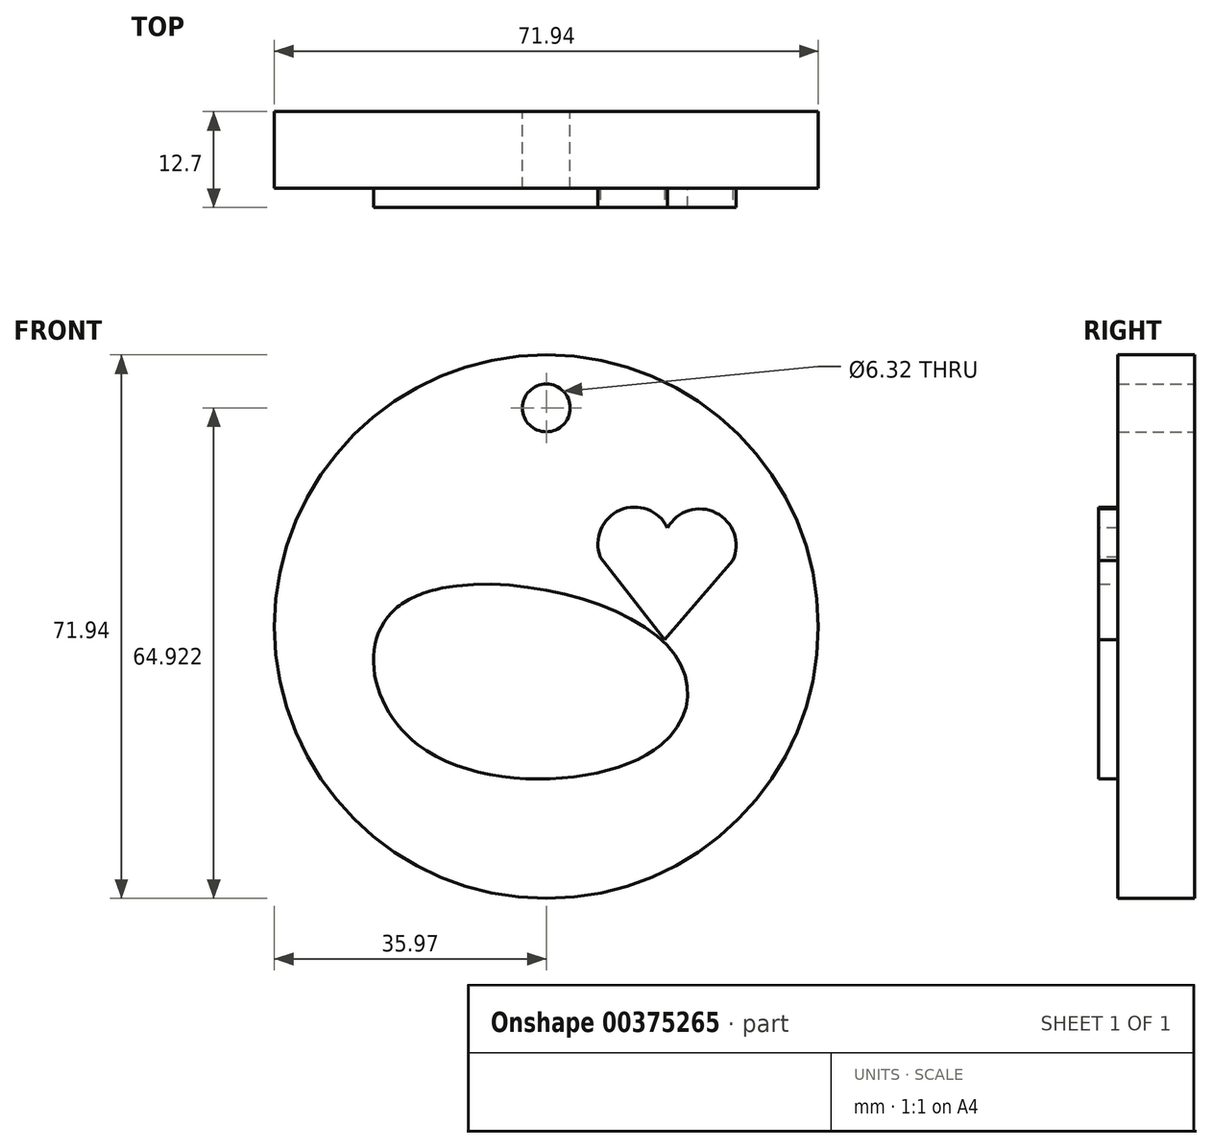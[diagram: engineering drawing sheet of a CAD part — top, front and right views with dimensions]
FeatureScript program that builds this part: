
annotation { "Feature Type Name" : "Feature", "Feature Type Description" : "" }
export const myFeature = defineFeature(function(context is Context, id is Id, definition is map)
    precondition{}
    {
        {
            var Q0;
            Q0=qCreatedBy(makeId("Front.planeOp"),FACE);
            var sketch = newSketch(context, id + "F0", { "sketchPlane" : qUnion([Q0])});
            skCircle(sketch, "E0", {"center": v(0, 0) * mm, "radius": 35.97 * mm});
            skSolve(sketch);
        }
        {
            var Q0;
            Q0=qSketchRegion(id+"F0",true);
            extrude(context, id + "F1", {"entities" : qUnion([Q0]), "depth" : 12.7 * mm});
        }
        {
            var Q0;
            Q0=makeQuery(id+"F1.opExtrude","CAP_FACE",FACE,{"disambiguationData":[OSD([sQuery(id+"F0.wireOp",EDGE,"E0")])],"isStart":false});
            var sketch = newSketch(context, id + "F2", { "sketchPlane" : qUnion([Q0])});
            skEllipticalArc(sketch, "E1", {});
            skPoint(sketch, "E2.2.internal.snap0", {"position": v(15.22, -15.6) * mm});
            skFitSpline(sketch, "E2", {"points": [v(-17, -15.6) * mm, v(15.22, -15.6) * mm, v(15.22, -1.73) * mm, v(-19.73, 2.56) * mm, v(-17, -15.6) * mm]});
            skArc(sketch, "E3", {"start": v(-17.8, 13.08) * mm, "mid": v(-24.21, 15.07) * mm, "end": v(-26.44, 8.74) * mm});
            skLineSegment(sketch, "E4", {"start": v(-26.44, 8.74) * mm, "end": v(-17.39, -1.73) * mm});
            skArc(sketch, "E5.MirrorCS", {"start": v(-17.8, 13.08) * mm, "mid": v(-11.5, 15.43) * mm, "end": v(-8.93, 9.22) * mm});
            skLineSegment(sketch, "E6.MirrorCS", {"start": v(-8.93, 9.22) * mm, "end": v(-17.39, -1.73) * mm});
            skArc(sketch, "E7.MirrorCS", {"start": v(16.02, 13.08) * mm, "mid": v(22.44, 15.07) * mm, "end": v(24.66, 8.74) * mm});
            skLineSegment(sketch, "E8.MirrorCS", {"start": v(24.66, 8.74) * mm, "end": v(15.61, -1.73) * mm});
            skLineSegment(sketch, "E9.MirrorCS", {"start": v(7.16, 9.22) * mm, "end": v(15.61, -1.73) * mm});
            skArc(sketch, "E10.MirrorCS", {"start": v(16.02, 13.08) * mm, "mid": v(9.73, 15.43) * mm, "end": v(7.16, 9.22) * mm});
            const initialGuessF2  = {"E1": [-0.0008881420638489816, -0.015604647807777988, 1, 0, 0.01610479690134306, 0.012966257095941073, 3.141592653589793, 0]};
            skSetInitialGuess(sketch, initialGuessF2);
            skSolve(sketch);
        }
        {
            var Q0;
            Q0=makeQuery(id+"F2.imprint","IMPRINT",FACE,{"disambiguationData":[TD([[makeQuery(id+"F2.imprint","IMPRINT",EDGE,{"derivedFrom":sQuery(id+"F2.wireOp",EDGE,"E7.MirrorCS")}),-1.0]])]});
            var Q1;
            Q1=makeQuery(id+"F2.imprint","IMPRINT",FACE,{"disambiguationData":[TD([[makeQuery(id+"F2.imprint","IMPRINT",EDGE,{"derivedFrom":sQuery(id+"F2.wireOp",EDGE,"E3")}),1.0]])]});
            var Q2;
            Q2=makeQuery(id+"F2.imprint","IMPRINT",FACE,{"disambiguationData":[TD([[makeQuery(id+"F2.imprint","IMPRINT",EDGE,{"derivedFrom":sQuery(id+"F2.wireOp",EDGE,"E1")}),1.0]])]});
            extrude(context, id + "F3", {"entities" : qUnion([Q0, Q1, Q2]), "operationType" : NewBodyOperationType.REMOVE, "oppositeDirection" : true, "depth" : 2.54 * mm});
        }
        {
            var Q0;
            Q0=qCreatedBy(makeId("Front.planeOp"),FACE);
            var sketch = newSketch(context, id + "F4", { "sketchPlane" : qUnion([Q0])});
            skCircle(sketch, "E11", {"center": v(0, 28.95) * mm, "radius": 3.16 * mm});
            skSolve(sketch);
        }
        {
            var Q0;
            Q0=makeQuery(id+"F4.imprint","IMPRINT",FACE,{"disambiguationData":[TD([[makeQuery(id+"F4.imprint","IMPRINT",EDGE,{"derivedFrom":sQuery(id+"F4.wireOp",EDGE,"E11")}),1.0]])]});
            extrude(context, id + "F5", {"entities" : qUnion([Q0]), "operationType" : NewBodyOperationType.REMOVE, "depth" : 12.7 * mm});
        }
    });
